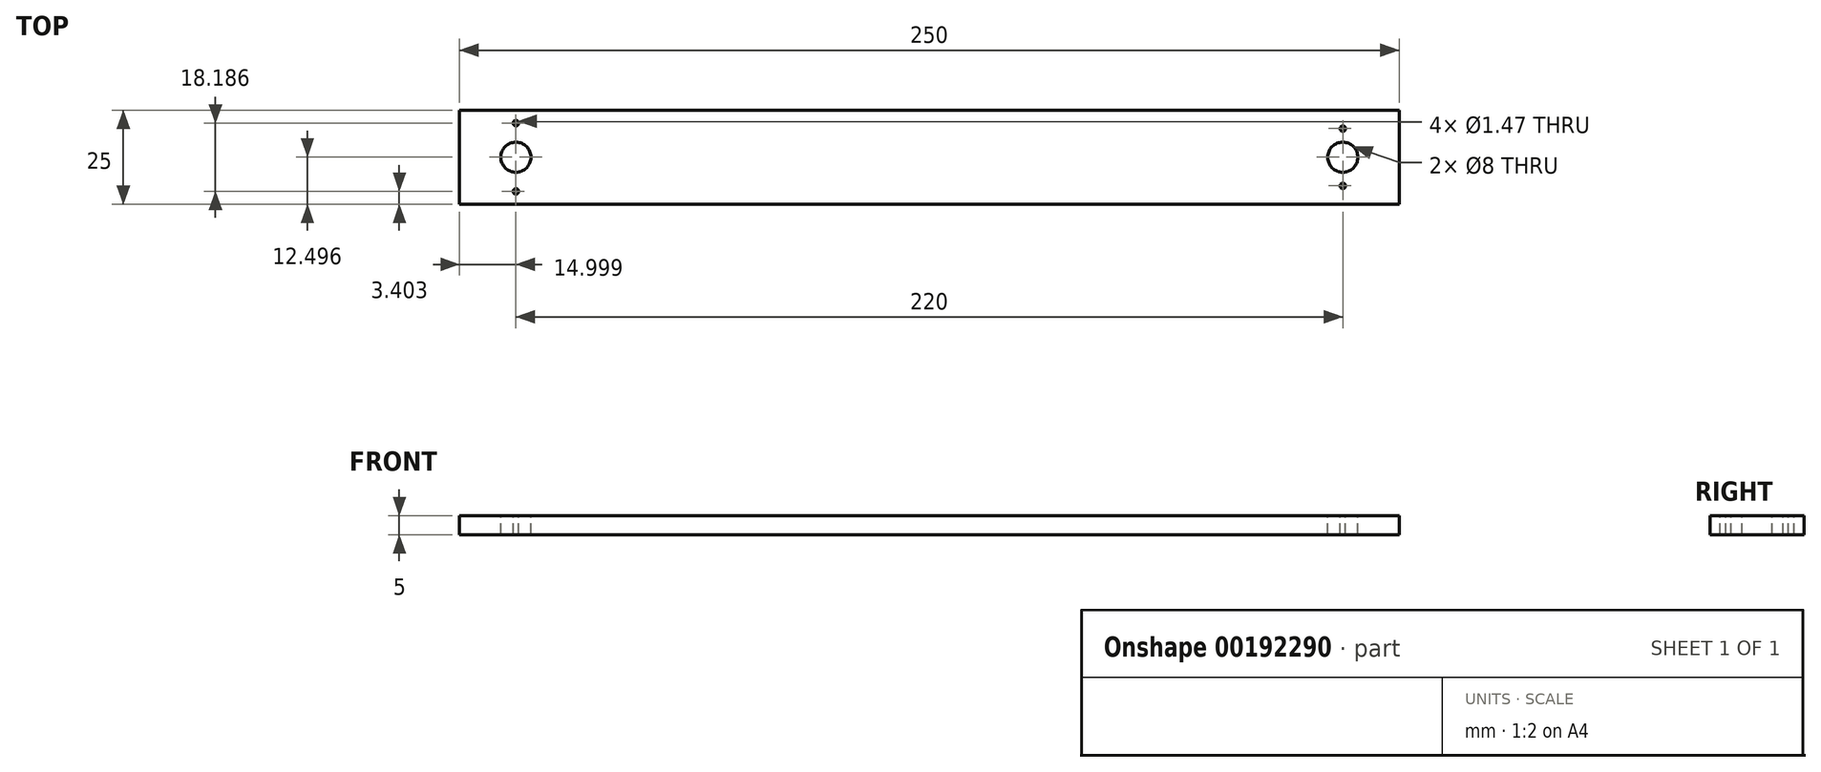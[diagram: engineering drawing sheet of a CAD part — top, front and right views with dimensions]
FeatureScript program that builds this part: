
annotation { "Feature Type Name" : "Feature", "Feature Type Description" : "" }
export const myFeature = defineFeature(function(context is Context, id is Id, definition is map)
    precondition{}
    {
        {
            var Q0;
            Q0=qCreatedBy(makeId("Top.planeOp"),FACE);
            var sketch = newSketch(context, id + "F0", { "sketchPlane" : qUnion([Q0])});
            skLineSegment(sketch, "E0.bottom", {"start": v(-113.3, -54.18) * mm, "end": v(136.7, -54.18) * mm});
            skLineSegment(sketch, "E0.top", {"start": v(-113.3, -79.18) * mm, "end": v(136.7, -79.18) * mm});
            skLineSegment(sketch, "E0.left", {"start": v(-113.3, -54.18) * mm, "end": v(-113.3, -79.18) * mm});
            skLineSegment(sketch, "E0.right", {"start": v(136.7, -54.18) * mm, "end": v(136.7, -79.18) * mm});
            skPoint(sketch, "E1", {"position": v(136.7, -54.18) * mm});
            skPoint(sketch, "E2", {"position": v(136.7, -79.18) * mm});
            skSolve(sketch);
        }
        {
            var Q0;
            Q0=makeQuery(id+"F0.imprint","IMPRINT",FACE,{"disambiguationData":[TD([[makeQuery(id+"F0.imprint","IMPRINT",EDGE,{"derivedFrom":sQuery(id+"F0.wireOp",EDGE,"E0.bottom")}),-1.0]])]});
            extrude(context, id + "F1", {"entities" : qUnion([Q0]), "depth" : 5 * mm});
        }
        {
            var Q0;
            Q0=makeQuery(id+"F1.opExtrude","CAP_FACE",FACE,{"disambiguationData":[OSD([sQuery(id+"F0.wireOp",EDGE,"E0.bottom"),sQuery(id+"F0.wireOp",EDGE,"E0.top"),sQuery(id+"F0.wireOp",EDGE,"E0.left"),sQuery(id+"F0.wireOp",EDGE,"E0.right")])],"isStart":false});
            var sketch = newSketch(context, id + "F2", { "sketchPlane" : qUnion([Q0])});
            skLineSegment(sketch, "E3.bottom", {"start": v(-113.3, -79.18) * mm, "end": v(-98.3, -79.18) * mm});
            skLineSegment(sketch, "E3.top", {"start": v(-113.3, -75.78) * mm, "end": v(-98.3, -75.78) * mm});
            skLineSegment(sketch, "E3.left", {"start": v(-113.3, -79.18) * mm, "end": v(-113.3, -75.78) * mm});
            skLineSegment(sketch, "E3.right", {"start": v(-98.3, -79.18) * mm, "end": v(-98.3, -75.78) * mm});
            skLineSegment(sketch, "E4.bottom", {"start": v(-113.3, -54.18) * mm, "end": v(-98.3, -54.18) * mm});
            skLineSegment(sketch, "E4.top", {"start": v(-113.3, -57.6) * mm, "end": v(-98.3, -57.6) * mm});
            skLineSegment(sketch, "E4.left", {"start": v(-113.3, -54.18) * mm, "end": v(-113.3, -57.6) * mm});
            skLineSegment(sketch, "E4.right", {"start": v(-98.3, -54.18) * mm, "end": v(-98.3, -57.6) * mm});
            skLineSegment(sketch, "E5.bottom", {"start": v(136.7, -54.18) * mm, "end": v(121.7, -54.18) * mm});
            skLineSegment(sketch, "E5.top", {"start": v(136.7, -59.06) * mm, "end": v(121.7, -59.06) * mm});
            skLineSegment(sketch, "E5.left", {"start": v(136.7, -54.18) * mm, "end": v(136.7, -59.06) * mm});
            skLineSegment(sketch, "E5.right", {"start": v(121.7, -54.18) * mm, "end": v(121.7, -59.06) * mm});
            skLineSegment(sketch, "E6.bottom", {"start": v(136.7, -79.18) * mm, "end": v(121.7, -79.18) * mm});
            skLineSegment(sketch, "E6.top", {"start": v(136.7, -74.3) * mm, "end": v(121.7, -74.3) * mm});
            skLineSegment(sketch, "E6.left", {"start": v(136.7, -79.18) * mm, "end": v(136.7, -74.3) * mm});
            skLineSegment(sketch, "E6.right", {"start": v(121.7, -79.18) * mm, "end": v(121.7, -74.3) * mm});
            skLineSegment(sketch, "E7", {"start": v(-98.3, -54.18) * mm, "end": v(-98.3, -66.68) * mm});
            skLineSegment(sketch, "E8", {"start": v(-98.3, -57.6) * mm, "end": v(-98.3, -66.68) * mm});
            skLineSegment(sketch, "E9", {"start": v(-98.3, -66.68) * mm, "end": v(-98.3, -75.78) * mm});
            skLineSegment(sketch, "E10", {"start": v(121.7, -54.18) * mm, "end": v(121.7, -66.68) * mm});
            skSolve(sketch);
        }
        {
            var Q0;
            Q0=sQuery(id+"F2.wireOp",VERTEX,"E4.right.end");
            var Q1;
            Q1=makeQuery(id+"F1.opExtrude","SWEPT_BODY",BODY,{"disambiguationData":[OSD([sQuery(id+"F0.wireOp",EDGE,"E0.bottom"),sQuery(id+"F0.wireOp",EDGE,"E0.top"),sQuery(id+"F0.wireOp",EDGE,"E0.left"),sQuery(id+"F0.wireOp",EDGE,"E0.right")])]});
            hole(context, id + "F3", {"style" : HoleStyle.SIMPLE, "endStyle" : HoleEndStyle.THROUGH, "holeDiameter" : 1.47 * mm, "locations" : qUnion([Q0]), "scope" : qUnion([Q1]), "isTappedThrough" : true});
        }
        {
            var Q0;
            Q0=sQuery(id+"F2.wireOp",VERTEX,"E3.top.end");
            var Q1;
            Q1=makeQuery(id+"F1.opExtrude","SWEPT_BODY",BODY,{"disambiguationData":[OSD([sQuery(id+"F0.wireOp",EDGE,"E0.bottom"),sQuery(id+"F0.wireOp",EDGE,"E0.top"),sQuery(id+"F0.wireOp",EDGE,"E0.left"),sQuery(id+"F0.wireOp",EDGE,"E0.right")])]});
            hole(context, id + "F4", {"style" : HoleStyle.SIMPLE, "endStyle" : HoleEndStyle.THROUGH, "holeDiameter" : 1.47 * mm, "locations" : qUnion([Q0]), "scope" : qUnion([Q1]), "isTappedThrough" : true});
        }
        {
            var Q0;
            Q0=sQuery(id+"F2.wireOp",VERTEX,"E5.top.end");
            var Q1;
            Q1=sQuery(id+"F2.wireOp",VERTEX,"E6.right.end");
            var Q2;
            Q2=makeQuery(id+"F1.opExtrude","SWEPT_BODY",BODY,{"disambiguationData":[OSD([sQuery(id+"F0.wireOp",EDGE,"E0.bottom"),sQuery(id+"F0.wireOp",EDGE,"E0.top"),sQuery(id+"F0.wireOp",EDGE,"E0.left"),sQuery(id+"F0.wireOp",EDGE,"E0.right")])]});
            hole(context, id + "F5", {"style" : HoleStyle.SIMPLE, "endStyle" : HoleEndStyle.THROUGH, "holeDiameter" : 1.47 * mm, "locations" : qUnion([Q0, Q1]), "scope" : qUnion([Q2]), "isTappedThrough" : true});
        }
        {
            var Q0;
            Q0=sQuery(id+"F2.wireOp",VERTEX,"E9.start");
            var Q1;
            Q1=sQuery(id+"F2.wireOp",VERTEX,"E10.end");
            var Q2;
            Q2=makeQuery(id+"F1.opExtrude","SWEPT_BODY",BODY,{"disambiguationData":[OSD([sQuery(id+"F0.wireOp",EDGE,"E0.bottom"),sQuery(id+"F0.wireOp",EDGE,"E0.top"),sQuery(id+"F0.wireOp",EDGE,"E0.left"),sQuery(id+"F0.wireOp",EDGE,"E0.right")])]});
            hole(context, id + "F6", {"style" : HoleStyle.SIMPLE, "endStyle" : HoleEndStyle.THROUGH, "holeDiameter" : 8 * mm, "locations" : qUnion([Q0, Q1]), "scope" : qUnion([Q2]), "isTappedThrough" : true});
        }
    });
